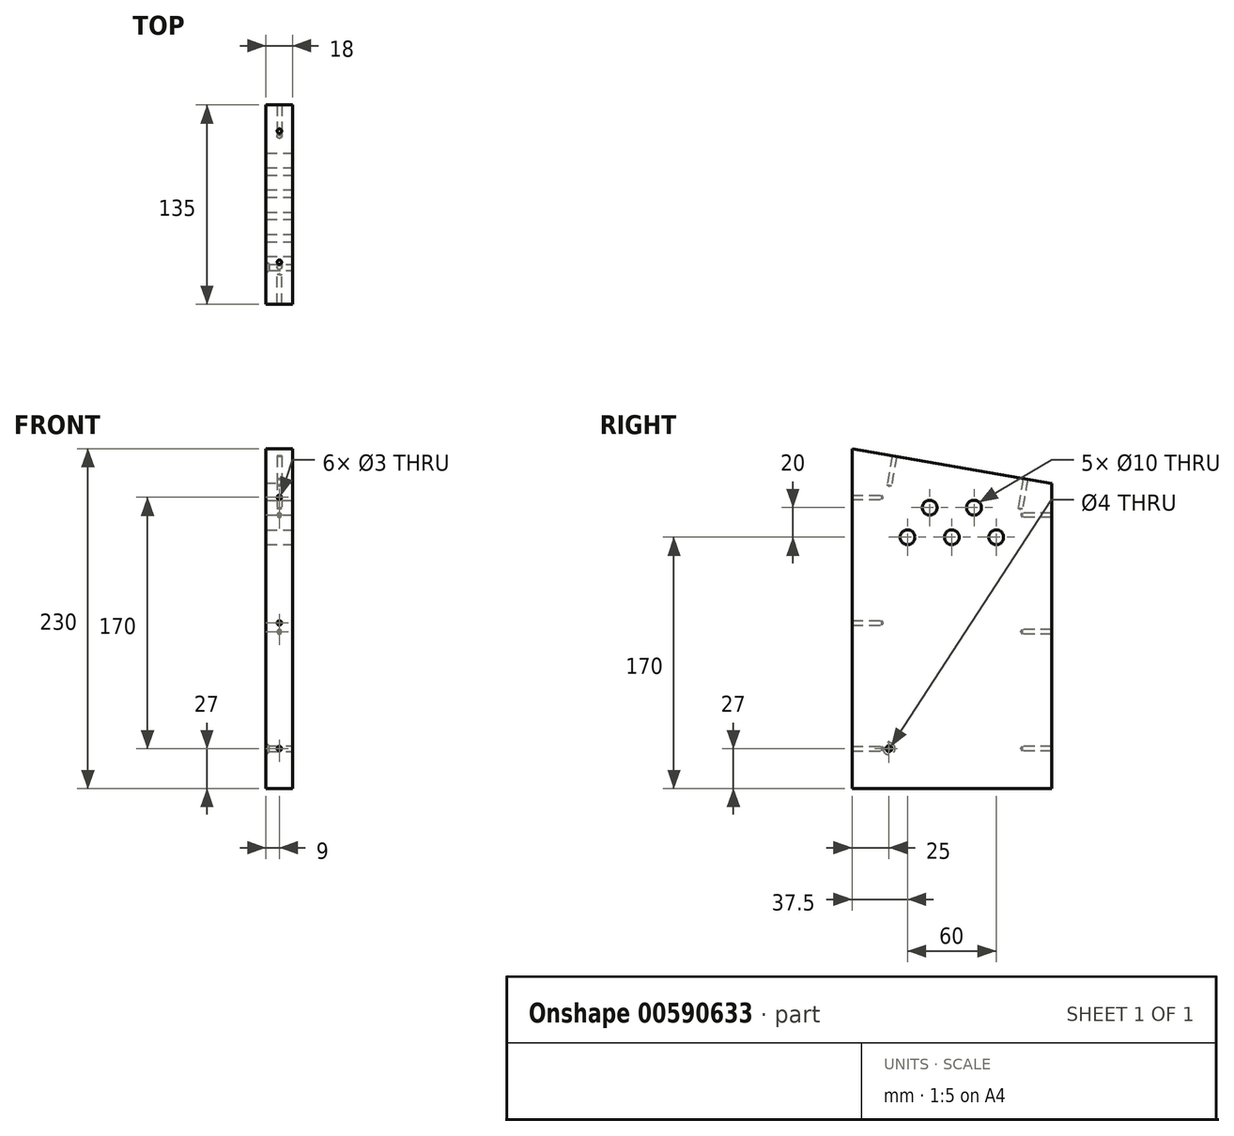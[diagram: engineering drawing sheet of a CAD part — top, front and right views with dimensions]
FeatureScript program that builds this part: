
annotation { "Feature Type Name" : "Feature", "Feature Type Description" : "" }
export const myFeature = defineFeature(function(context is Context, id is Id, definition is map)
    precondition{}
    {
        {
            var Q0;
            Q0=qCreatedBy(makeId("Right.planeOp"),FACE);
            var sketch = newSketch(context, id + "F0", { "sketchPlane" : qUnion([Q0])});
            skLineSegment(sketch, "E0", {"start": v(0, 0) * mm, "end": v(0, 230) * mm});
            skLineSegment(sketch, "E1", {"start": v(0, 230) * mm, "end": v(135, 206.2) * mm});
            skLineSegment(sketch, "E2", {"start": v(135, 206.2) * mm, "end": v(135, 0) * mm});
            skLineSegment(sketch, "E3", {"start": v(135, 0) * mm, "end": v(0, 0) * mm});
            skPoint(sketch, "E4", {"position": v(67.5, 170) * mm});
            skPoint(sketch, "E5", {"position": v(37.5, 170) * mm});
            skPoint(sketch, "E6", {"position": v(97.5, 170) * mm});
            skPoint(sketch, "E7", {"position": v(52.5, 190) * mm});
            skPoint(sketch, "E8", {"position": v(82.5, 190) * mm});
            skPoint(sketch, "E9", {"position": v(25, 27) * mm});
            skPoint(sketch, "E10", {"position": v(67.5, 0) * mm});
            skSolve(sketch);
        }
        {
            var Q0;
            Q0=makeQuery(id+"F0.imprint","IMPRINT",FACE,{"disambiguationData":[TD([[makeQuery(id+"F0.imprint","IMPRINT",EDGE,{"derivedFrom":sQuery(id+"F0.wireOp",EDGE,"E0")}),-1.0]])]});
            extrude(context, id + "F1", {"entities" : qUnion([Q0]), "depth" : 18 * mm, "offsetDistance" : 25 * mm});
        }
        {
            var Q0;
            Q0=sQuery(id+"F0.wireOp",VERTEX,"E5");
            var Q1;
            Q1=sQuery(id+"F0.wireOp",VERTEX,"E4");
            var Q2;
            Q2=sQuery(id+"F0.wireOp",VERTEX,"E6");
            var Q3;
            Q3=makeQuery(id+"F1.opExtrude","SWEPT_BODY",BODY,{"disambiguationData":[OSD([sQuery(id+"F0.wireOp",EDGE,"E0"),sQuery(id+"F0.wireOp",EDGE,"E1"),sQuery(id+"F0.wireOp",EDGE,"E2"),sQuery(id+"F0.wireOp",EDGE,"E3")])]});
            hole(context, id + "F2", {"style" : HoleStyle.SIMPLE, "endStyle" : HoleEndStyle.THROUGH, "oppositeDirection" : true, "holeDiameter" : 10 * mm, "majorDiameter" : 5 * mm, "isTappedThrough" : true, "tappedDepth" : 12 * mm, "tapClearance" : 3, "locations" : qUnion([Q0, Q1, Q2]), "scope" : qUnion([Q3])});
        }
        {
            var Q0;
            Q0=sQuery(id+"F0.wireOp",VERTEX,"E7");
            var Q1;
            Q1=sQuery(id+"F0.wireOp",VERTEX,"E8");
            var Q2;
            Q2=makeQuery(id+"F1.opExtrude","SWEPT_BODY",BODY,{"disambiguationData":[OSD([sQuery(id+"F0.wireOp",EDGE,"E0"),sQuery(id+"F0.wireOp",EDGE,"E1"),sQuery(id+"F0.wireOp",EDGE,"E2"),sQuery(id+"F0.wireOp",EDGE,"E3")])]});
            hole(context, id + "F3", {"style" : HoleStyle.SIMPLE, "endStyle" : HoleEndStyle.THROUGH, "oppositeDirection" : true, "holeDiameter" : 10 * mm, "majorDiameter" : 5 * mm, "isTappedThrough" : true, "tappedDepth" : 12 * mm, "tapClearance" : 3, "locations" : qUnion([Q0, Q1]), "scope" : qUnion([Q2])});
        }
        {
            var Q0;
            Q0=sQuery(id+"F0.wireOp",VERTEX,"E9");
            var Q1;
            Q1=makeQuery(id+"F1.opExtrude","SWEPT_BODY",BODY,{"disambiguationData":[OSD([sQuery(id+"F0.wireOp",EDGE,"E0"),sQuery(id+"F0.wireOp",EDGE,"E1"),sQuery(id+"F0.wireOp",EDGE,"E2"),sQuery(id+"F0.wireOp",EDGE,"E3")])]});
            hole(context, id + "F4", {"style" : HoleStyle.C_SINK, "endStyle" : HoleEndStyle.THROUGH, "oppositeDirection" : true, "holeDiameter" : 4 * mm, "cSinkDiameter" : 8.2 * mm, "cSinkAngle" : 90 * degree, "majorDiameter" : 5 * mm, "isTappedThrough" : true, "tappedDepth" : 12 * mm, "tapClearance" : 3, "locations" : qUnion([Q0]), "scope" : qUnion([Q1])});
        }
        {
            var Q0;
            Q0=makeQuery(id+"F1.opExtrude","SWEPT_FACE",FACE,{"disambiguationData":[OSD([sQuery(id+"F0.wireOp",EDGE,"E2")])]});
            var sketch = newSketch(context, id + "F5", { "sketchPlane" : qUnion([Q0])});
            skPoint(sketch, "E11", {"position": v(-9, 27) * mm});
            skPoint(sketch, "E11.positionSnap0", {"position": v(-9, 0) * mm});
            skPoint(sketch, "E12", {"position": v(-9, 106) * mm});
            skPoint(sketch, "E13", {"position": v(-9, 185) * mm});
            skSolve(sketch);
        }
        {
            var Q0;
            Q0=sQuery(id+"F5.wireOp",VERTEX,"E11");
            var Q1;
            Q1=sQuery(id+"F5.wireOp",VERTEX,"E12");
            var Q2;
            Q2=sQuery(id+"F5.wireOp",VERTEX,"E13");
            var Q3;
            Q3=makeQuery(id+"F1.opExtrude","SWEPT_BODY",BODY,{"disambiguationData":[OSD([sQuery(id+"F0.wireOp",EDGE,"E0"),sQuery(id+"F0.wireOp",EDGE,"E1"),sQuery(id+"F0.wireOp",EDGE,"E2"),sQuery(id+"F0.wireOp",EDGE,"E3")])]});
            hole(context, id + "F6", {"style" : HoleStyle.SIMPLE, "endStyle" : HoleEndStyle.BLIND, "holeDiameter" : 3 * mm, "majorDiameter" : 5 * mm, "holeDepth" : 20 * mm, "isTappedThrough" : true, "tappedDepth" : 12 * mm, "tapClearance" : 3, "locations" : qUnion([Q0, Q1, Q2]), "scope" : qUnion([Q3])});
        }
        {
            var Q0;
            Q0=makeQuery(id+"F1.opExtrude","SWEPT_FACE",FACE,{"disambiguationData":[OSD([sQuery(id+"F0.wireOp",EDGE,"E0")])]});
            var sketch = newSketch(context, id + "F7", { "sketchPlane" : qUnion([Q0])});
            skPoint(sketch, "E14", {"position": v(9, 27) * mm});
            skPoint(sketch, "E14.positionSnap0", {"position": v(9, 0) * mm});
            skPoint(sketch, "E15", {"position": v(9, 112) * mm});
            skPoint(sketch, "E16", {"position": v(9, 197) * mm});
            skSolve(sketch);
        }
        {
            var Q0;
            Q0=sQuery(id+"F7.wireOp",VERTEX,"E14");
            var Q1;
            Q1=sQuery(id+"F7.wireOp",VERTEX,"E15");
            var Q2;
            Q2=sQuery(id+"F7.wireOp",VERTEX,"E16");
            var Q3;
            Q3=makeQuery(id+"F1.opExtrude","SWEPT_BODY",BODY,{"disambiguationData":[OSD([sQuery(id+"F0.wireOp",EDGE,"E0"),sQuery(id+"F0.wireOp",EDGE,"E1"),sQuery(id+"F0.wireOp",EDGE,"E2"),sQuery(id+"F0.wireOp",EDGE,"E3")])]});
            hole(context, id + "F8", {"style" : HoleStyle.SIMPLE, "endStyle" : HoleEndStyle.BLIND, "holeDiameter" : 3 * mm, "majorDiameter" : 5 * mm, "holeDepth" : 20 * mm, "isTappedThrough" : true, "tappedDepth" : 12 * mm, "tapClearance" : 3, "locations" : qUnion([Q0, Q1, Q2]), "scope" : qUnion([Q3])});
        }
        {
            var Q0;
            Q0=makeQuery(id+"F1.opExtrude","SWEPT_FACE",FACE,{"disambiguationData":[OSD([sQuery(id+"F0.wireOp",EDGE,"E1")])]});
            var sketch = newSketch(context, id + "F9", { "sketchPlane" : qUnion([Q0])});
            skPoint(sketch, "E17", {"position": v(9, 79.14) * mm});
            skPoint(sketch, "E17.positionSnap0", {"position": v(9, 97.14) * mm});
            skPoint(sketch, "E18", {"position": v(9, -10.86) * mm});
            skSolve(sketch);
        }
        {
            var Q0;
            Q0=sQuery(id+"F9.wireOp",VERTEX,"E18");
            var Q1;
            Q1=sQuery(id+"F9.wireOp",VERTEX,"E17");
            var Q2;
            Q2=makeQuery(id+"F1.opExtrude","SWEPT_BODY",BODY,{"disambiguationData":[OSD([sQuery(id+"F0.wireOp",EDGE,"E0"),sQuery(id+"F0.wireOp",EDGE,"E1"),sQuery(id+"F0.wireOp",EDGE,"E2"),sQuery(id+"F0.wireOp",EDGE,"E3")])]});
            hole(context, id + "F10", {"style" : HoleStyle.SIMPLE, "endStyle" : HoleEndStyle.BLIND, "holeDiameter" : 3 * mm, "majorDiameter" : 5 * mm, "holeDepth" : 20 * mm, "isTappedThrough" : true, "tappedDepth" : 12 * mm, "tapClearance" : 3, "locations" : qUnion([Q0, Q1]), "scope" : qUnion([Q2])});
        }
    });
